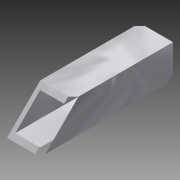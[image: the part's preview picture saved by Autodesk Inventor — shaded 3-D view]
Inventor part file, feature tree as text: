
AUTODESK INVENTOR PART (.ipt)
format: ipt  version: 2015 SP1 (Build 190203100, 203)  size: 109,568 bytes
history: native  units: in
note: dims shown in document units (in); Inventor stores cm internally (conversion verified against a paired STEP export)
features: extrude x2, sketch x2
ambient origin geometry x8: Origin, YZ Plane, XZ Plane, XY Plane, X Axis, Y Axis, Z Axis, Center Point
bodies: Solid1 (feature_tree)
feature tree (4):
  extrude  "Extrusion1"  Depth=1.0in
  extrude  "Extrusion2"  Depth=0.75in
  sketch  "Sketch1"  dims[d0=1.0in d1=1.0in]
  sketch  "Sketch2"  dims[d2=0.75in d3=0.75in d4=0.125in d5=0.125in d6=4.0in d7=0.0in d8=135.0deg d9=3.0in d10=0.0in]
